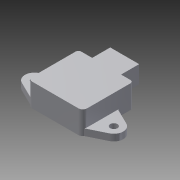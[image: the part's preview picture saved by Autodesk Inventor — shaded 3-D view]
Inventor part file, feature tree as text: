
AUTODESK INVENTOR PART (.ipt)
format: ipt  version: 2015 (Build 190159000, 159)  size: 208,896 bytes
history: native  units: mm
features: extrude x7, sketch x5, chamfer x2, projected_geometry x1
ambient origin geometry x8: Origin, YZ Plane, XZ Plane, XY Plane, X Axis, Y Axis, Z Axis, Center Point
bodies: Solid1 (feature_tree)
feature tree (15):
  sketch  "Sketch1"  dims[d0=38.0mm d1=35.0mm]
  extrude  "Extrusion1"  Depth=35.0mm
  extrude  "Extrusion2"  Depth=2.0mm
  extrude  "Extrusion3"  Depth=13.0mm
  chamfer  "Chamfer1"  Distance=13.0mm
  sketch  "Sketch3"  dims[d4=3.0mm d5=13.0mm]
  extrude  "Extrusion4"  Depth=0.5mm
  extrude  "Extrusion5"  Depth=2.0mm
  extrude  "Extrusion6"  Depth=0.5mm
  chamfer  "Chamfer3"  Distance=4.537856mm
  extrude  "Extrusion7"  Depth=13.0mm
  sketch  "Sketch2"  dims[d2=55.0mm d3=2.0mm]
  projected_geometry  "Projected Loop1"
  sketch  "Sketch4"  dims[d6=4.5mm]
  sketch  "Sketch5"  dims[d7=5.0mm d8=13.0mm d9=4.363323mm d12=2.0mm d13=4.537856mm d14=4.537856mm d15=13.0mm d16=4.537856mm d17=4.537856mm d18=2.0mm d19=4.6mm d20=0.0mm d21=16.0mm d22=0.0mm d24=16.0mm d25=15.1mm d26=2.0mm d27=0.0mm d28=0.5mm d29=2.0mm d30=45.0deg d31=8.0mm d32=2.0mm d33=2.0mm d34=12.0mm d35=0.0mm d39=9.7mm d40=20.0mm d41=13.0mm d42=0.0mm d43=8.0mm d44=6.0mm d45=0.0mm d46=1.0mm d47=1.99mm d48=45.0deg d49=0.5mm d50=0.0mm]
